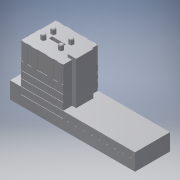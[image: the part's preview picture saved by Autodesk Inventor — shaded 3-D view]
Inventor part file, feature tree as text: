
AUTODESK INVENTOR PART (.ipt)
format: ipt  version: 2018.3 (Build 223284000, 284)  size: 551,424 bytes
history: native  units: mm
features: extrude x19, sketch x19, pattern_linear x3, chamfer x1
ambient origin geometry x8: Origin, YZ Plane, XZ Plane, XY Plane, X Axis, Y Axis, Z Axis, Center Point
bodies: Solid1 (feature_tree)
feature tree (42):
  extrude  "Extrusion1"  Depth=28.01mm
  extrude  "Extrusion2"  Depth=0.31mm
  extrude  "Extrusion3"  Depth=8.81mm
  extrude  "Extrusion4"  Depth=33.64mm
  extrude  "Extrusion5"  Depth=31.92mm TaperAngle=0.0deg
  pattern_linear  "Rectangular Pattern1"  Count1=9 Spacing1=6.25mm
  extrude  "Extrusion6"  Depth=33.96mm
  extrude  "Extrusion7"  Depth=7.78mm
  pattern_linear  "Rectangular Pattern2"  Spacing1=0.31mm  [1 undecoded]
  extrude  "Extrusion8"  Depth=6.25mm
  extrude  "Extrusion9"  Depth=0.31mm TaperAngle=0.0deg
  extrude  "Extrusion10"  Depth=5.26mm
  extrude  "Extrusion11"  Depth=26.61mm
  pattern_linear  "Rectangular Pattern3"  Spacing1=2.59mm  [1 undecoded]
  extrude  "Extrusion12"  Depth=2.09mm
  extrude  "Extrusion13"  Depth=1.25mm TaperAngle=0.0deg
  extrude  "Extrusion14"  Depth=1.24mm TaperAngle=0.0deg
  extrude  "Extrusion15"  Depth=3.13mm
  extrude  "Extrusion16"  Depth=2.5mm
  extrude  "Extrusion17"  Depth=0.31mm TaperAngle=0.0deg
  sketch  "Sketch18"  dims[d31=3.13mm d32=7.78mm]
  extrude  "Extrusion18"  Depth=20.0mm
  sketch  "Sketch19"  dims[d33=0.31mm d34=0.0mm d35=0.31mm d36=0.0mm d37=90.0mm d39=6.25mm d40=0.31mm d41=0.0mm d42=5.26mm d43=26.61mm d44=2.59mm d45=2.09mm d46=1.25mm d47=0.0mm d48=1.24mm d49=0.0mm d50=3.13mm d51=2.5mm d52=0.31mm d53=0.0mm d54=20.0mm d56=5.63mm d57=4.07mm d58=2.5mm d59=0.31mm d60=0.0mm d61=3.1mm d62=4.61mm d63=4.61mm d64=3.1mm d65=14.1mm d66=0.0mm d67=0.31mm d68=0.0mm d69=0.31mm d70=0.0mm d71=0.31mm d72=0.0mm d73=4.38mm d74=4.38mm d75=4.38mm d76=12.39mm d77=0.7mm d78=0.7mm d79=0.31mm d80=0.0mm d81=33.64mm d82=26.93mm d83=20.0mm d84=14.0mm d85=6.69mm d86=6.7mm d87=5.1mm d88=5.1mm d89=2.15mm d90=1.13mm d91=1.1mm d92=2.15mm d94=1.1mm d95=12.11mm d96=1.131227mm d97=2.15mm d98=2.15mm d99=1.45mm d100=1.45mm d101=1.13mm d102=1.131mm d103=4.83298mm d104=12.110227mm d105=11.0mm d106=2.6mm d107=4.5mm d108=5.7mm d109=4.0mm d110=0.0mm d111=11.0mm d112=2.6mm d113=12.4mm d114=9.592268mm d115=40.0mm d116=0.0mm d117=0.5mm d118=2.0mm d119=45.0deg]
  extrude  "Extrusion19"  Depth=4.07mm
  chamfer  "Chamfer1"  Distance=2.5mm
  sketch  "Sketch1"  dims[d0=100.0mm d1=28.01mm]
  sketch  "Sketch2"  dims[d2=13.41mm d3=0.0mm d4=0.31mm]
  sketch  "Sketch3"  dims[d5=0.31mm d6=8.81mm]
  sketch  "Sketch4"  dims[d7=57.55mm d8=33.64mm]
  sketch  "Sketch5"  dims[d9=27.39mm d10=31.92mm d11=0.0mm]
  sketch  "Sketch6"  dims[d12=6.8mm]
  sketch  "Sketch7"  dims[d13=6.8mm]
  sketch  "Sketch8"  dims[d14=3.35mm]
  sketch  "Sketch9"  dims[d15=34.21mm d16=0.0mm]
  sketch  "Sketch10"  dims[d17=3.44mm d18=0.0mm]
  sketch  "Sketch11"  dims[d19=2.5mm]
  sketch  "Sketch12"  dims[d20=1.25mm]
  sketch  "Sketch13"  dims[d21=1.25mm]
  sketch  "Sketch14"  dims[d22=3.13mm]
  sketch  "Sketch15"  dims[d23=2.95mm]
  sketch  "Sketch16"  dims[d24=0.31mm d25=0.0mm d26=90.0mm d28=6.25mm]
  sketch  "Sketch17"  dims[d29=3.35mm d30=33.96mm]
note: 2 required parameter values undecoded (feature->parameter linkage not recoverable at this tier; creation-order binding heuristic only, values carry confidence <= 0.55)
